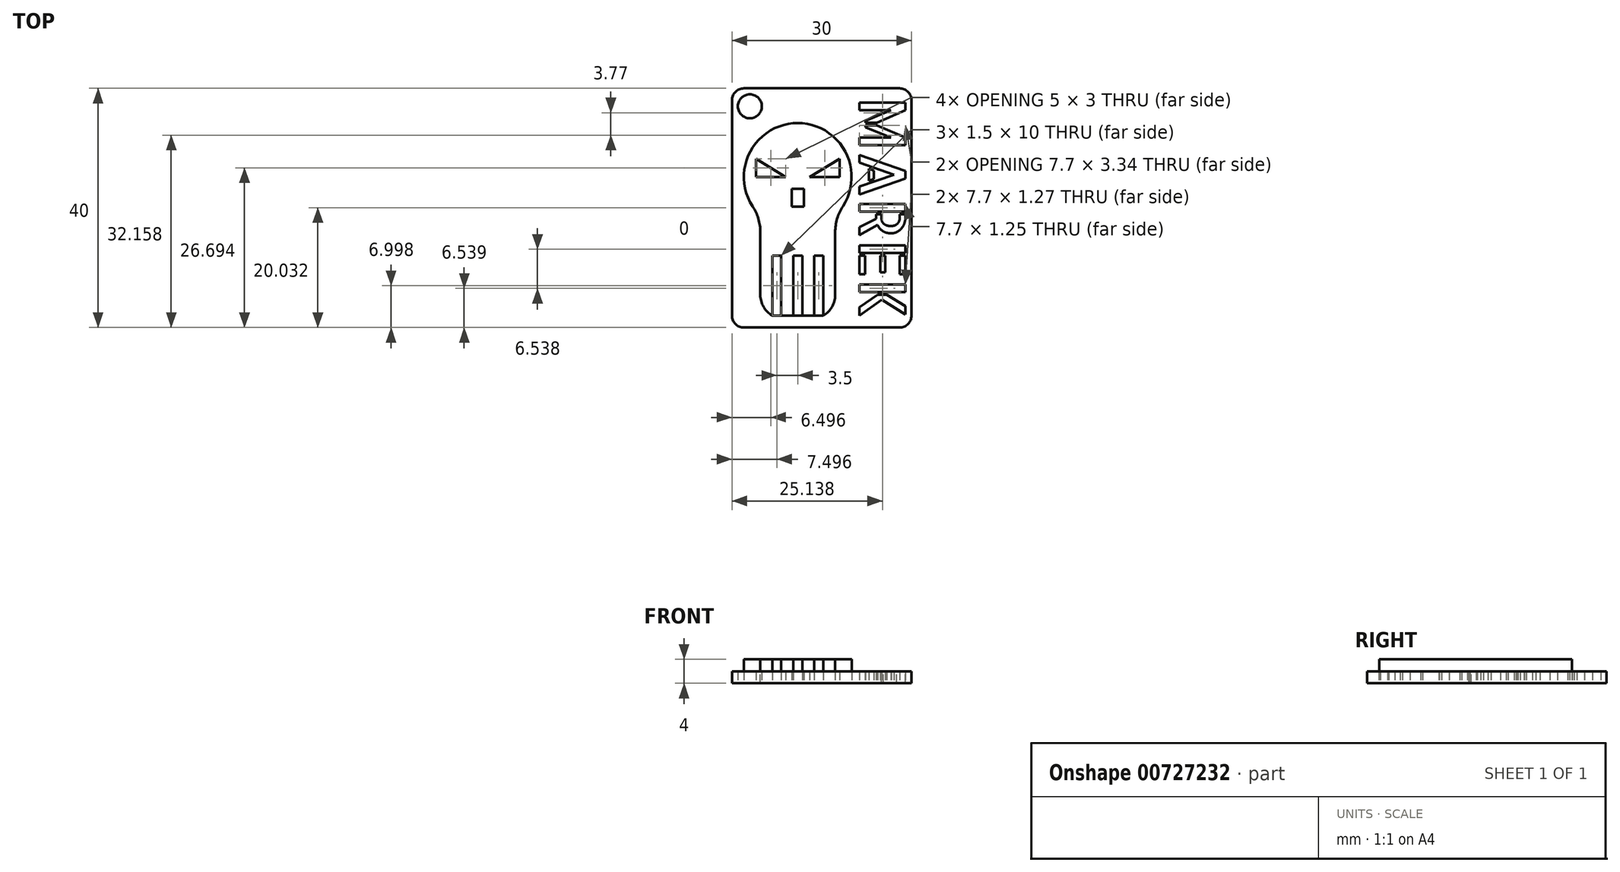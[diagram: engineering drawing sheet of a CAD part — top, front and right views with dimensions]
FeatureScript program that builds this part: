
annotation { "Feature Type Name" : "Feature", "Feature Type Description" : "" }
export const myFeature = defineFeature(function(context is Context, id is Id, definition is map)
    precondition{}
    {
        {
            var Q0;
            Q0=qCreatedBy(makeId("Top.planeOp"),FACE);
            var sketch = newSketch(context, id + "F0", { "sketchPlane" : qUnion([Q0])});
            skLineSegment(sketch, "E0.bottom", {"start": v(-36.07, 30.2) * mm, "end": v(-6.07, 30.2) * mm});
            skLineSegment(sketch, "E0.top", {"start": v(-36.07, -9.8) * mm, "end": v(-6.07, -9.8) * mm});
            skLineSegment(sketch, "E0.left", {"start": v(-36.07, 30.2) * mm, "end": v(-36.07, -9.8) * mm});
            skLineSegment(sketch, "E0.right", {"start": v(-6.07, 30.2) * mm, "end": v(-6.07, -9.8) * mm});
            skSolve(sketch);
        }
        {
            var Q0;
            Q0=qCreatedBy(makeId("Top.planeOp"),FACE);
            var sketch = newSketch(context, id + "F1", { "sketchPlane" : qUnion([Q0])});
            skCircle(sketch, "E1", {"center": v(-33.07, 27.2) * mm, "radius": 2 * mm});
            skSolve(sketch);
        }
        {
            var Q0;
            Q0=qCreatedBy(makeId("Top.planeOp"),FACE);
            var sketch = newSketch(context, id + "F2", { "sketchPlane" : qUnion([Q0])});
            skText(sketch, "E2", { "text": "MAREK", "fontName": "AllertaStencil-Regular.ttf"});
            const initialGuessF2  = {"E2": [-0.01478, 0.02876, 0, -1, 0.0077]};
            skSetInitialGuess(sketch, initialGuessF2);
            skSolve(sketch);
        }
        {
            var Q0;
            Q0=qCreatedBy(makeId("Top.planeOp"),FACE);
            var sketch = newSketch(context, id + "F3", { "sketchPlane" : qUnion([Q0])});
            skArc(sketch, "E3", {"start": v(-18.82, 8.92) * mm, "mid": v(-25.07, 24.4) * mm, "end": v(-31.32, 8.92) * mm});
            skLineSegment(sketch, "E4", {"start": v(-25.07, 2.2) * mm, "end": v(-24.32, 2.2) * mm});
            skLineSegment(sketch, "E5", {"start": v(-24.32, 2.2) * mm, "end": v(-24.32, -7.8) * mm});
            skLineSegment(sketch, "E6", {"start": v(-25.07, 2.2) * mm, "end": v(-25.82, 2.2) * mm});
            skLineSegment(sketch, "E7", {"start": v(-25.82, 2.2) * mm, "end": v(-25.82, -7.8) * mm});
            skLineSegment(sketch, "E8", {"start": v(-25.82, -7.8) * mm, "end": v(-27.82, -7.8) * mm});
            skLineSegment(sketch, "E9", {"start": v(-27.82, -7.8) * mm, "end": v(-27.82, 2.2) * mm});
            skLineSegment(sketch, "E10", {"start": v(-27.82, 2.2) * mm, "end": v(-29.32, 2.2) * mm});
            skLineSegment(sketch, "E11", {"start": v(-29.32, 2.2) * mm, "end": v(-29.32, -7.8) * mm});
            skLineSegment(sketch, "E12", {"start": v(-29.32, -7.8) * mm, "end": v(-31.32, -7.8) * mm});
            skLineSegment(sketch, "E13", {"start": v(-31.32, -7.8) * mm, "end": v(-31.32, 2.2) * mm});
            skLineSegment(sketch, "E14", {"start": v(-24.32, -7.8) * mm, "end": v(-22.32, -7.8) * mm});
            skLineSegment(sketch, "E15", {"start": v(-22.32, -7.8) * mm, "end": v(-22.32, 2.2) * mm});
            skLineSegment(sketch, "E16", {"start": v(-22.32, 2.2) * mm, "end": v(-20.82, 2.2) * mm});
            skLineSegment(sketch, "E17", {"start": v(-20.82, 2.2) * mm, "end": v(-20.82, -7.8) * mm});
            skLineSegment(sketch, "E18", {"start": v(-20.82, -7.8) * mm, "end": v(-18.82, -7.8) * mm});
            skLineSegment(sketch, "E19", {"start": v(-18.82, -7.8) * mm, "end": v(-18.82, 1) * mm});
            skLineSegment(sketch, "E20", {"start": v(-18.82, 1) * mm, "end": v(-18.82, 8.92) * mm});
            skLineSegment(sketch, "E21", {"start": v(-31.32, 2.2) * mm, "end": v(-31.32, 8.92) * mm});
            skLineSegment(sketch, "E22", {"start": v(-27.07, 15.4) * mm, "end": v(-32.07, 15.4) * mm});
            skLineSegment(sketch, "E23", {"start": v(-32.07, 15.4) * mm, "end": v(-32.07, 18.4) * mm});
            skLineSegment(sketch, "E24", {"start": v(-32.07, 18.4) * mm, "end": v(-27.07, 15.4) * mm});
            skLineSegment(sketch, "E25", {"start": v(-23.07, 15.4) * mm, "end": v(-18.07, 15.4) * mm});
            skLineSegment(sketch, "E26", {"start": v(-18.07, 15.4) * mm, "end": v(-18.07, 18.4) * mm});
            skLineSegment(sketch, "E27", {"start": v(-18.07, 18.4) * mm, "end": v(-23.07, 15.4) * mm});
            skLineSegment(sketch, "E28", {"start": v(-24.07, 13.4) * mm, "end": v(-24.07, 10.4) * mm});
            skLineSegment(sketch, "E29", {"start": v(-24.07, 10.4) * mm, "end": v(-26.07, 10.4) * mm});
            skLineSegment(sketch, "E30", {"start": v(-26.07, 10.4) * mm, "end": v(-26.07, 13.4) * mm});
            skLineSegment(sketch, "E31", {"start": v(-29.32, -7.8) * mm, "end": v(-27.82, -7.8) * mm});
            skLineSegment(sketch, "E32", {"start": v(-25.82, -7.8) * mm, "end": v(-24.32, -7.8) * mm});
            skLineSegment(sketch, "E33", {"start": v(-22.32, -7.8) * mm, "end": v(-20.82, -7.8) * mm});
            skLineSegment(sketch, "E34", {"start": v(-26.07, 13.4) * mm, "end": v(-25.07, 13.4) * mm});
            skLineSegment(sketch, "E35", {"start": v(-25.07, 13.4) * mm, "end": v(-24.07, 13.4) * mm});
            skSolve(sketch);
        }
        {
            var Q0;
            Q0 = qSketchRegion(id + "F0", true);
            extrude(context, id + "F4", {"entities" : qUnion([Q0]), "depth" : 2 * mm, "offsetDistance" : 25 * mm});
        }
        {
            var Q0;
            Q0 = qSketchRegion(id + "F1", true);
            extrude(context, id + "F5", {"entities" : qUnion([Q0]), "operationType" : NewBodyOperationType.REMOVE, "depth" : 4 * mm, "offsetDistance" : 25 * mm});
        }
        {
            var Q0;
            Q0 = qSketchRegion(id + "F2", true);
            extrude(context, id + "F6", {"entities" : qUnion([Q0]), "operationType" : NewBodyOperationType.REMOVE, "depth" : 4 * mm, "offsetDistance" : 25 * mm});
        }
        {
            var Q0;
            Q0 = qSketchRegion(id + "F3", true);
            extrude(context, id + "F7", {"entities" : qUnion([Q0]), "depth" : 4 * mm, "offsetDistance" : 25 * mm});
        }
        {
            var Q0;
            Q0=makeQuery(id+"F7.opExtrude","SWEPT_EDGE",EDGE,{"disambiguationData":[OSD([sQuery(id+"F3.wireOp",EDGE,"E3"),sQuery(id+"F3.wireOp",EDGE,"E20")])]});
            var Q1;
            Q1=makeQuery(id+"F7.opExtrude","SWEPT_EDGE",EDGE,{"disambiguationData":[OSD([sQuery(id+"F3.wireOp",EDGE,"E3"),sQuery(id+"F3.wireOp",EDGE,"E21")])]});
            fillet(context, id + "F8", {"entities" : qUnion([Q0, Q1]), "radius" : 8 * mm, "tangentPropagation" : true, "allowEdgeOverflow" : false});
        }
        {
            var Q0;
            Q0=makeQuery(id+"F3.imprint","IMPRINT",FACE,{"disambiguationData":[TD([[makeQuery(id+"F3.imprint","IMPRINT",EDGE,{"derivedFrom":sQuery(id+"F3.wireOp",EDGE,"E25")}),1.0]])]});
            extrude(context, id + "F9", {"entities" : qUnion([Q0]), "operationType" : NewBodyOperationType.REMOVE, "depth" : 4 * mm, "offsetDistance" : 25 * mm});
        }
        {
            var Q0;
            Q0=makeQuery(id+"F3.imprint","IMPRINT",FACE,{"disambiguationData":[TD([[makeQuery(id+"F3.imprint","IMPRINT",EDGE,{"derivedFrom":sQuery(id+"F3.wireOp",EDGE,"E22")}),-1.0]])]});
            extrude(context, id + "F10", {"entities" : qUnion([Q0]), "operationType" : NewBodyOperationType.REMOVE, "depth" : 4 * mm, "offsetDistance" : 25 * mm});
        }
        {
            var Q0;
            Q0=makeQuery(id+"F3.imprint","IMPRINT",FACE,{"disambiguationData":[TD([[makeQuery(id+"F3.imprint","IMPRINT",EDGE,{"derivedFrom":sQuery(id+"F3.wireOp",EDGE,"E28")}),-1.0]])]});
            extrude(context, id + "F11", {"entities" : qUnion([Q0]), "operationType" : NewBodyOperationType.REMOVE, "depth" : 4 * mm, "offsetDistance" : 25 * mm});
        }
        {
            var Q0;
            Q0=makeQuery(id+"F3.imprint","IMPRINT",FACE,{"disambiguationData":[TD([[makeQuery(id+"F3.imprint","IMPRINT",EDGE,{"derivedFrom":sQuery(id+"F3.wireOp",EDGE,"E9")}),1.0]])]});
            var Q1;
            Q1=makeQuery(id+"F3.imprint","IMPRINT",FACE,{"disambiguationData":[TD([[makeQuery(id+"F3.imprint","IMPRINT",EDGE,{"derivedFrom":sQuery(id+"F3.wireOp",EDGE,"E4")}),-1.0]])]});
            var Q2;
            Q2=makeQuery(id+"F3.imprint","IMPRINT",FACE,{"disambiguationData":[TD([[makeQuery(id+"F3.imprint","IMPRINT",EDGE,{"derivedFrom":sQuery(id+"F3.wireOp",EDGE,"E15")}),-1.0]])]});
            extrude(context, id + "F12", {"entities" : qUnion([Q0, Q1, Q2]), "operationType" : NewBodyOperationType.REMOVE, "depth" : 4 * mm, "offsetDistance" : 25 * mm});
        }
        {
            var Q0;
            Q0=makeQuery(id+"F7.opExtrude","SWEPT_EDGE",EDGE,{"disambiguationData":[OSD([sQuery(id+"F3.wireOp",EDGE,"E12"),sQuery(id+"F3.wireOp",EDGE,"E13")])]});
            var Q1;
            Q1=makeQuery(id+"F7.opExtrude","SWEPT_EDGE",EDGE,{"disambiguationData":[OSD([sQuery(id+"F3.wireOp",EDGE,"E18"),sQuery(id+"F3.wireOp",EDGE,"E19")])]});
            fillet(context, id + "F13", {"entities" : qUnion([Q0, Q1]), "radius" : 4 * mm, "tangentPropagation" : true, "allowEdgeOverflow" : false});
        }
        {
            var Q0;
            Q0=makeQuery(id+"F4.opExtrude","SWEPT_EDGE",EDGE,{"disambiguationData":[OSD([sQuery(id+"F0.wireOp",EDGE,"E0.top"),sQuery(id+"F0.wireOp",EDGE,"E0.left")])]});
            var Q1;
            Q1=makeQuery(id+"F4.opExtrude","SWEPT_EDGE",EDGE,{"disambiguationData":[OSD([sQuery(id+"F0.wireOp",EDGE,"E0.top"),sQuery(id+"F0.wireOp",EDGE,"E0.right")])]});
            var Q2;
            Q2=makeQuery(id+"F4.opExtrude","SWEPT_EDGE",EDGE,{"disambiguationData":[OSD([sQuery(id+"F0.wireOp",EDGE,"E0.bottom"),sQuery(id+"F0.wireOp",EDGE,"E0.left")])]});
            var Q3;
            Q3=makeQuery(id+"F4.opExtrude","SWEPT_EDGE",EDGE,{"disambiguationData":[OSD([sQuery(id+"F0.wireOp",EDGE,"E0.bottom"),sQuery(id+"F0.wireOp",EDGE,"E0.right")])]});
            fillet(context, id + "F14", {"entities" : qUnion([Q0, Q1, Q2, Q3]), "radius" : 2 * mm, "tangentPropagation" : true, "allowEdgeOverflow" : false});
        }
    });
